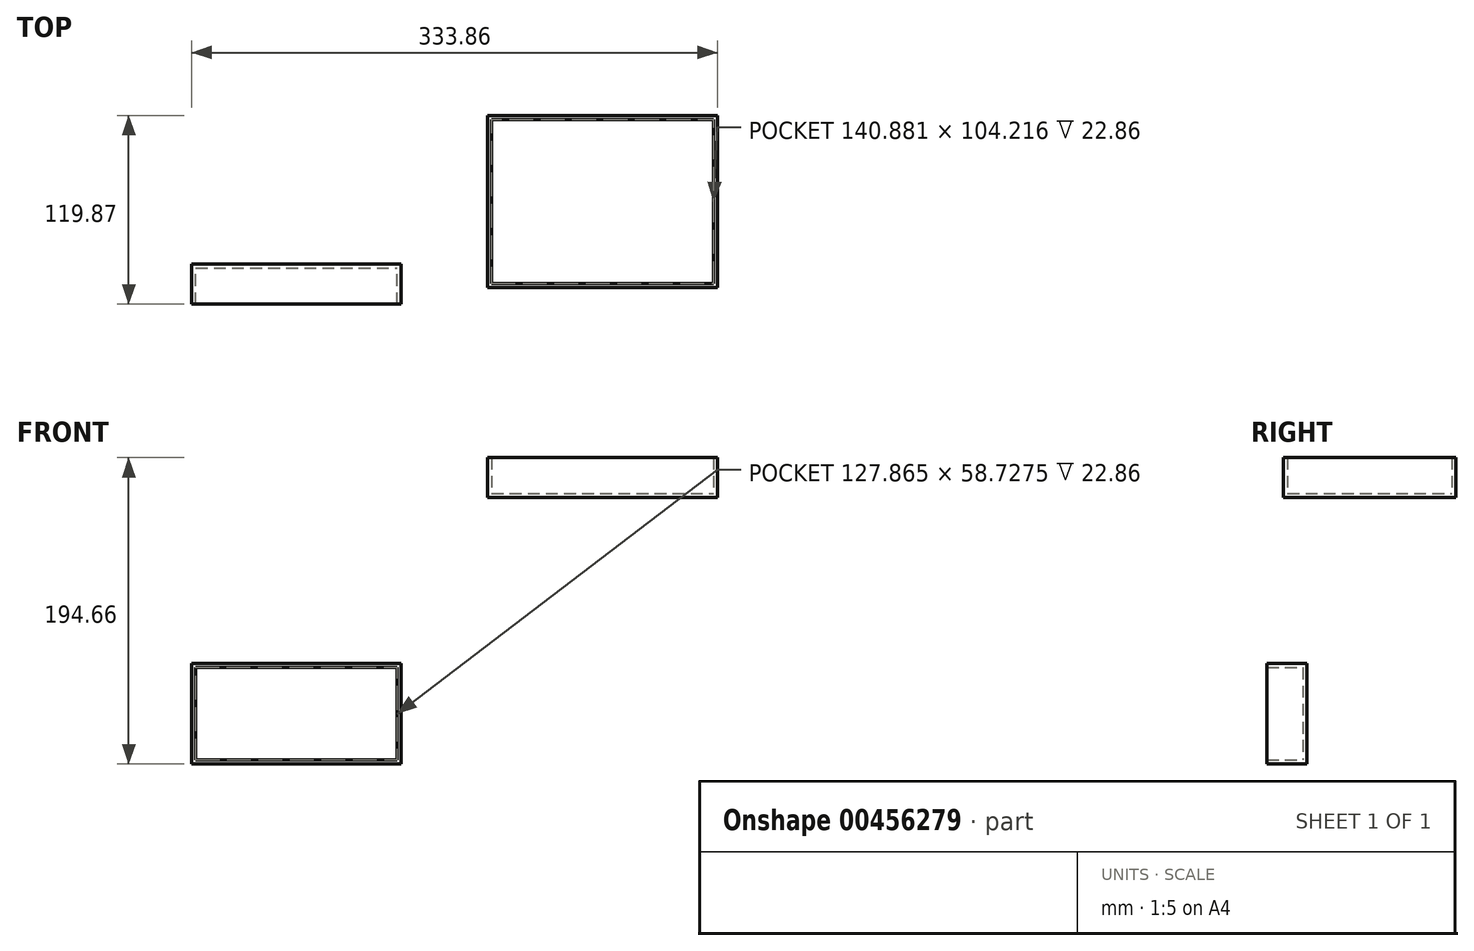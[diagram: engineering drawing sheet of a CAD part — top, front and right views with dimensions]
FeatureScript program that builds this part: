
annotation { "Feature Type Name" : "Feature", "Feature Type Description" : "" }
export const myFeature = defineFeature(function(context is Context, id is Id, definition is map)
    precondition{}
    {
        {
            var Q0;
            Q0=qCreatedBy(makeId("Top.planeOp"),FACE);
            var sketch = newSketch(context, id + "F0", { "sketchPlane" : qUnion([Q0])});
            skLineSegment(sketch, "E0.bottom", {"start": v(-71.73, -14.82) * mm, "end": v(74.23, -14.82) * mm});
            skLineSegment(sketch, "E0.top", {"start": v(-71.73, 94.47) * mm, "end": v(74.23, 94.47) * mm});
            skLineSegment(sketch, "E0.left", {"start": v(-71.73, -14.82) * mm, "end": v(-71.73, 94.47) * mm});
            skLineSegment(sketch, "E0.right", {"start": v(74.23, -14.82) * mm, "end": v(74.23, 94.47) * mm});
            skSolve(sketch);
        }
        {
            var Q0;
            Q0 = qSketchRegion(id + "F0", true);
            extrude(context, id + "F1", {"entities" : qUnion([Q0]), "depth" : 25.4 * mm});
        }
        {
            var Q0;
            Q0=makeQuery(id+"F1.opExtrude","CAP_FACE",FACE,{"disambiguationData":[OSD([sQuery(id+"F0.wireOp",EDGE,"E0.bottom"),sQuery(id+"F0.wireOp",EDGE,"E0.top"),sQuery(id+"F0.wireOp",EDGE,"E0.left"),sQuery(id+"F0.wireOp",EDGE,"E0.right")])],"isStart":false});
            shell(context, id + "F2", {"entities" : qUnion([Q0]), "thickness" : 2.54 * mm});
        }
        {
            var Q0;
            Q0=qCreatedBy(makeId("Front.planeOp"),FACE);
            var sketch = newSketch(context, id + "F3", { "sketchPlane" : qUnion([Q0])});
            skLineSegment(sketch, "E1.bottom", {"start": v(-259.63, -105.45) * mm, "end": v(-126.69, -105.45) * mm});
            skLineSegment(sketch, "E1.top", {"start": v(-259.63, -169.26) * mm, "end": v(-126.69, -169.26) * mm});
            skLineSegment(sketch, "E1.left", {"start": v(-259.63, -105.45) * mm, "end": v(-259.63, -169.26) * mm});
            skLineSegment(sketch, "E1.right", {"start": v(-126.69, -105.45) * mm, "end": v(-126.69, -169.26) * mm});
            skSolve(sketch);
        }
        {
            var Q0;
            Q0 = qSketchRegion(id + "F3", true);
            extrude(context, id + "F4", {"entities" : qUnion([Q0]), "depth" : 25.4 * mm});
        }
        {
            var Q0;
            Q0=makeQuery(id+"F4.opExtrude","CAP_FACE",FACE,{"disambiguationData":[OSD([sQuery(id+"F3.wireOp",EDGE,"E1.bottom"),sQuery(id+"F3.wireOp",EDGE,"E1.top"),sQuery(id+"F3.wireOp",EDGE,"E1.left"),sQuery(id+"F3.wireOp",EDGE,"E1.right")])],"isStart":false});
            shell(context, id + "F5", {"entities" : qUnion([Q0]), "thickness" : 2.54 * mm});
        }
    });
